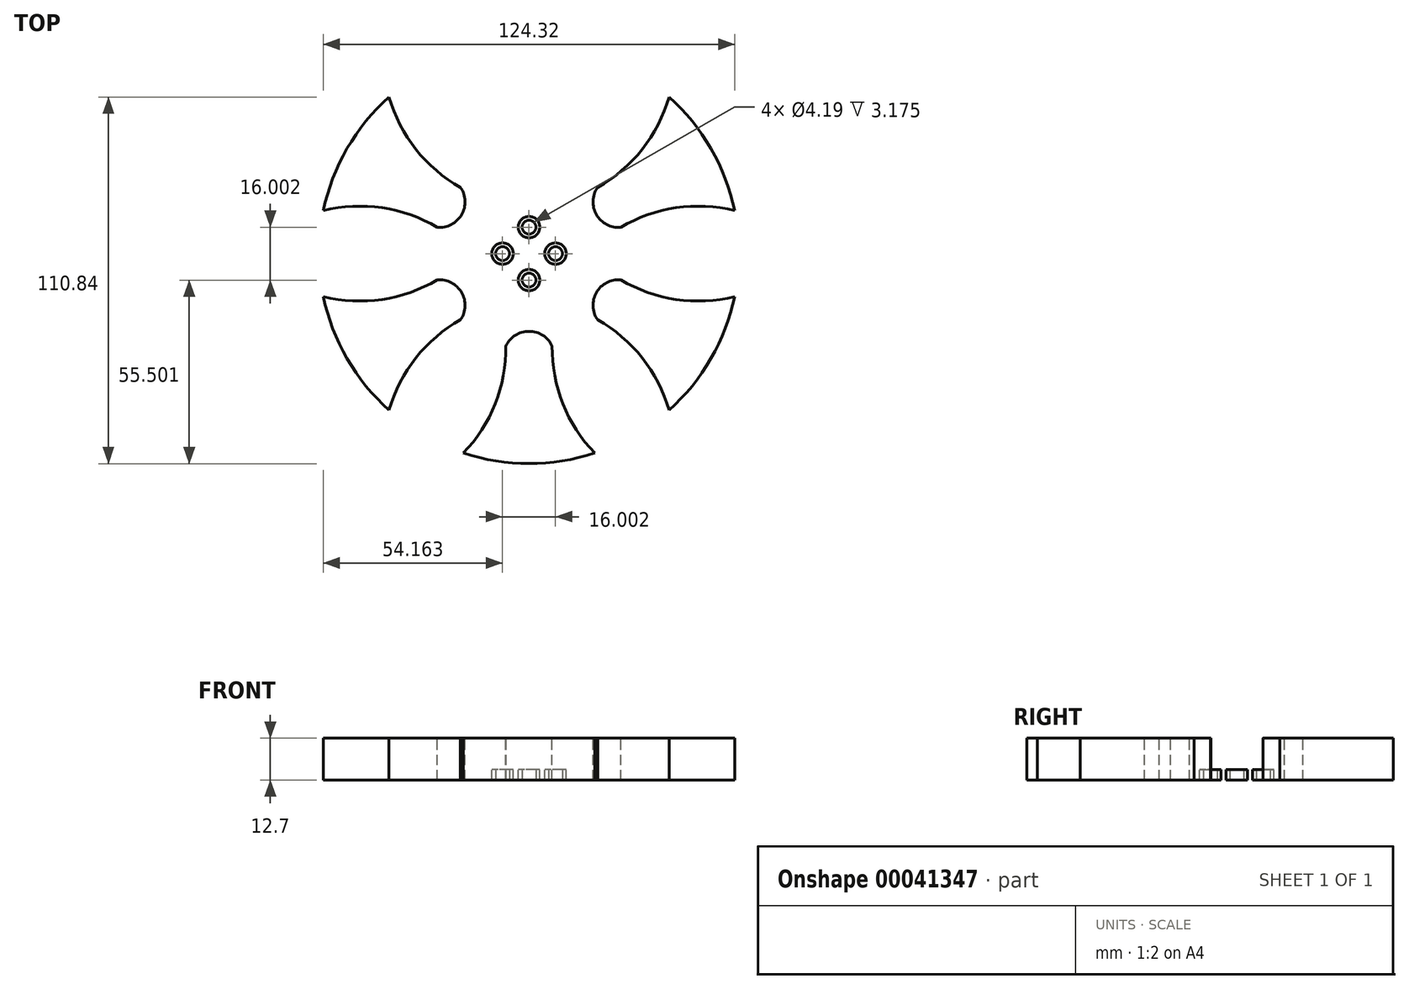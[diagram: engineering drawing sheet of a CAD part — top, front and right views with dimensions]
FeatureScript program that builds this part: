
annotation { "Feature Type Name" : "Feature", "Feature Type Description" : "" }
export const myFeature = defineFeature(function(context is Context, id is Id, definition is map)
    precondition{}
    {
        {
            var Q0;
            Q0=qCreatedBy(makeId("Top.planeOp"),FACE);
            var sketch = newSketch(context, id + "F0", { "sketchPlane" : qUnion([Q0])});
            skCircle(sketch, "E0", {"center": v(-27.84, 11.05) * mm, "radius": 63.5 * mm});
            skCircle(sketch, "E1", {"center": v(-27.84, 11.05) * mm, "radius": 4.06 * mm});
            skCircle(sketch, "E2", {"center": v(-27.84, 19.05) * mm, "radius": 2.1 * mm});
            skCircle(sketch, "E3", {"center": v(-19.84, 11.05) * mm, "radius": 2.1 * mm});
            skCircle(sketch, "E4", {"center": v(-27.84, 3.05) * mm, "radius": 2.1 * mm});
            skCircle(sketch, "E5", {"center": v(-35.84, 11.05) * mm, "radius": 2.1 * mm});
            skSolve(sketch);
        }
        {
            var Q0;
            Q0 = qSketchRegion(id + "F0", true);
            extrude(context, id + "F1", {"entities" : qUnion([Q0]), "depth" : 12.7 * mm});
        }
        {
            var Q0;
            Q0=makeQuery(id+"F1.opExtrude","CAP_FACE",FACE,{"disambiguationData":[OSD([sQuery(id+"F0.wireOp",EDGE,"E0"),sQuery(id+"F0.wireOp",EDGE,"E1"),sQuery(id+"F0.wireOp",EDGE,"E2"),sQuery(id+"F0.wireOp",EDGE,"E3"),sQuery(id+"F0.wireOp",EDGE,"E4"),sQuery(id+"F0.wireOp",EDGE,"E5")])],"isStart":false});
            var sketch = newSketch(context, id + "F2", { "sketchPlane" : qUnion([Q0])});
            skCircle(sketch, "E6", {"center": v(-27.84, 19.05) * mm, "radius": 3.24 * mm});
            skCircle(sketch, "E7", {"center": v(-19.84, 11.05) * mm, "radius": 3.24 * mm});
            skCircle(sketch, "E8", {"center": v(-27.84, 3.05) * mm, "radius": 3.24 * mm});
            skCircle(sketch, "E9", {"center": v(-35.84, 11.05) * mm, "radius": 3.24 * mm});
            skArc(sketch, "E10", {"start": v(-8, 71.37) * mm, "mid": v(-17.62, 56.45) * mm, "end": v(-20.85, 39) * mm});
            skArc(sketch, "E11.MirrorCS", {"start": v(-47.68, 71.37) * mm, "mid": v(-38.05, 56.45) * mm, "end": v(-34.82, 39) * mm});
            skArc(sketch, "E12", {"start": v(-34.82, 39) * mm, "mid": v(-27.84, 34.57) * mm, "end": v(-20.85, 39) * mm});
            skArc(sketch, "E13.1.0", {"start": v(-90, 24.03) * mm, "mid": v(-72.26, 24.9) * mm, "end": v(-55.53, 18.97) * mm});
            skArc(sketch, "E13.1.1", {"start": v(-55.53, 18.97) * mm, "mid": v(-48.2, 22.8) * mm, "end": v(-48.54, 31.07) * mm});
            skArc(sketch, "E13.1.2", {"start": v(-70.15, 58.4) * mm, "mid": v(-62.04, 42.6) * mm, "end": v(-48.54, 31.07) * mm});
            skArc(sketch, "E13.2.0", {"start": v(-70.15, -36.3) * mm, "mid": v(-62.04, -20.5) * mm, "end": v(-48.54, -8.97) * mm});
            skArc(sketch, "E13.2.1", {"start": v(-48.54, -8.97) * mm, "mid": v(-48.2, -0.7) * mm, "end": v(-55.53, 3.13) * mm});
            skArc(sketch, "E13.2.2", {"start": v(-90, -1.93) * mm, "mid": v(-72.26, -2.8) * mm, "end": v(-55.53, 3.13) * mm});
            skArc(sketch, "E13.3.0", {"start": v(-8, -49.27) * mm, "mid": v(-17.62, -34.35) * mm, "end": v(-20.85, -16.89) * mm});
            skArc(sketch, "E13.3.1", {"start": v(-20.85, -16.89) * mm, "mid": v(-27.84, -12.46) * mm, "end": v(-34.82, -16.89) * mm});
            skArc(sketch, "E13.3.2", {"start": v(-47.68, -49.27) * mm, "mid": v(-38.05, -34.35) * mm, "end": v(-34.82, -16.89) * mm});
            skArc(sketch, "E13.4.0", {"start": v(34.32, -1.93) * mm, "mid": v(16.59, -2.8) * mm, "end": v(-0.15, 3.13) * mm});
            skArc(sketch, "E13.4.1", {"start": v(-0.15, 3.13) * mm, "mid": v(-7.47, -0.7) * mm, "end": v(-7.13, -8.97) * mm});
            skArc(sketch, "E13.4.2", {"start": v(14.48, -36.3) * mm, "mid": v(6.37, -20.5) * mm, "end": v(-7.13, -8.97) * mm});
            skArc(sketch, "E13.5.0", {"start": v(14.48, 58.4) * mm, "mid": v(6.37, 42.6) * mm, "end": v(-7.13, 31.07) * mm});
            skArc(sketch, "E13.5.1", {"start": v(-7.13, 31.07) * mm, "mid": v(-7.47, 22.8) * mm, "end": v(-0.15, 18.97) * mm});
            skArc(sketch, "E13.5.2", {"start": v(34.32, 24.03) * mm, "mid": v(16.59, 24.9) * mm, "end": v(-0.15, 18.97) * mm});
            skPoint(sketch, "E13.center", {"position": v(-27.84, 11.05) * mm});
            skPoint(sketch, "E14.trimOffspring.start.orphan", {"position": v(-27.84, 39) * mm});
            skSolve(sketch);
        }
        {
            var Q0;
            {var subQ0=sQuery(id+"F2.wireOp",EDGE,"E13.1.0");Q0=makeQuery(id+"F2.imprint","IMPRINT",FACE,{"disambiguationData":[TD([[makeQuery(id+"F2.imprint","IMPRINT",EDGE,{"derivedFrom":subQ0}),1.0]])]});}
            var Q1;
            {var subQ0=sQuery(id+"F2.wireOp",EDGE,"E10");Q1=makeQuery(id+"F2.imprint","IMPRINT",FACE,{"disambiguationData":[TD([[makeQuery(id+"F2.imprint","IMPRINT",EDGE,{"derivedFrom":subQ0}),-1.0]])]});}
            var Q2;
            {var subQ0=sQuery(id+"F2.wireOp",EDGE,"E13.5.0");Q2=makeQuery(id+"F2.imprint","IMPRINT",FACE,{"disambiguationData":[TD([[makeQuery(id+"F2.imprint","IMPRINT",EDGE,{"derivedFrom":subQ0}),1.0]])]});}
            var Q3;
            {var subQ0=sQuery(id+"F2.wireOp",EDGE,"E13.4.0");Q3=makeQuery(id+"F2.imprint","IMPRINT",FACE,{"disambiguationData":[TD([[makeQuery(id+"F2.imprint","IMPRINT",EDGE,{"derivedFrom":subQ0}),1.0]])]});}
            var Q4;
            {var subQ0=sQuery(id+"F2.wireOp",EDGE,"E13.3.0");Q4=makeQuery(id+"F2.imprint","IMPRINT",FACE,{"disambiguationData":[TD([[makeQuery(id+"F2.imprint","IMPRINT",EDGE,{"derivedFrom":subQ0}),1.0]])]});}
            var Q5;
            {var subQ0=sQuery(id+"F2.wireOp",EDGE,"E13.2.0");Q5=makeQuery(id+"F2.imprint","IMPRINT",FACE,{"disambiguationData":[TD([[makeQuery(id+"F2.imprint","IMPRINT",EDGE,{"derivedFrom":subQ0}),1.0]])]});}
            extrude(context, id + "F3", {"entities" : qUnion([Q0, Q1, Q2, Q3, Q4, Q5]), "operationType" : NewBodyOperationType.REMOVE, "oppositeDirection" : true, "depth" : 12.7 * mm});
        }
        {
            var Q0;
            Q0=makeQuery(id+"F2.imprint","IMPRINT",FACE,{"disambiguationData":[TD([[makeQuery(id+"F2.imprint","IMPRINT",EDGE,{"derivedFrom":sQuery(id+"F2.wireOp",EDGE,"E6")}),1.0]])]});
            var Q1;
            Q1=makeQuery(id+"F2.imprint","IMPRINT",FACE,{"disambiguationData":[TD([[makeQuery(id+"F2.imprint","IMPRINT",EDGE,{"derivedFrom":sQuery(id+"F2.wireOp",EDGE,"E7")}),1.0]])]});
            var Q2;
            Q2=makeQuery(id+"F2.imprint","IMPRINT",FACE,{"disambiguationData":[TD([[makeQuery(id+"F2.imprint","IMPRINT",EDGE,{"derivedFrom":sQuery(id+"F2.wireOp",EDGE,"E8")}),1.0]])]});
            var Q3;
            Q3=makeQuery(id+"F2.imprint","IMPRINT",FACE,{"disambiguationData":[TD([[makeQuery(id+"F2.imprint","IMPRINT",EDGE,{"derivedFrom":sQuery(id+"F2.wireOp",EDGE,"E9")}),1.0]])]});
            extrude(context, id + "F4", {"entities" : qUnion([Q0, Q1, Q2, Q3]), "operationType" : NewBodyOperationType.REMOVE, "oppositeDirection" : true, "depth" : 9.52 * mm});
        }
    });
